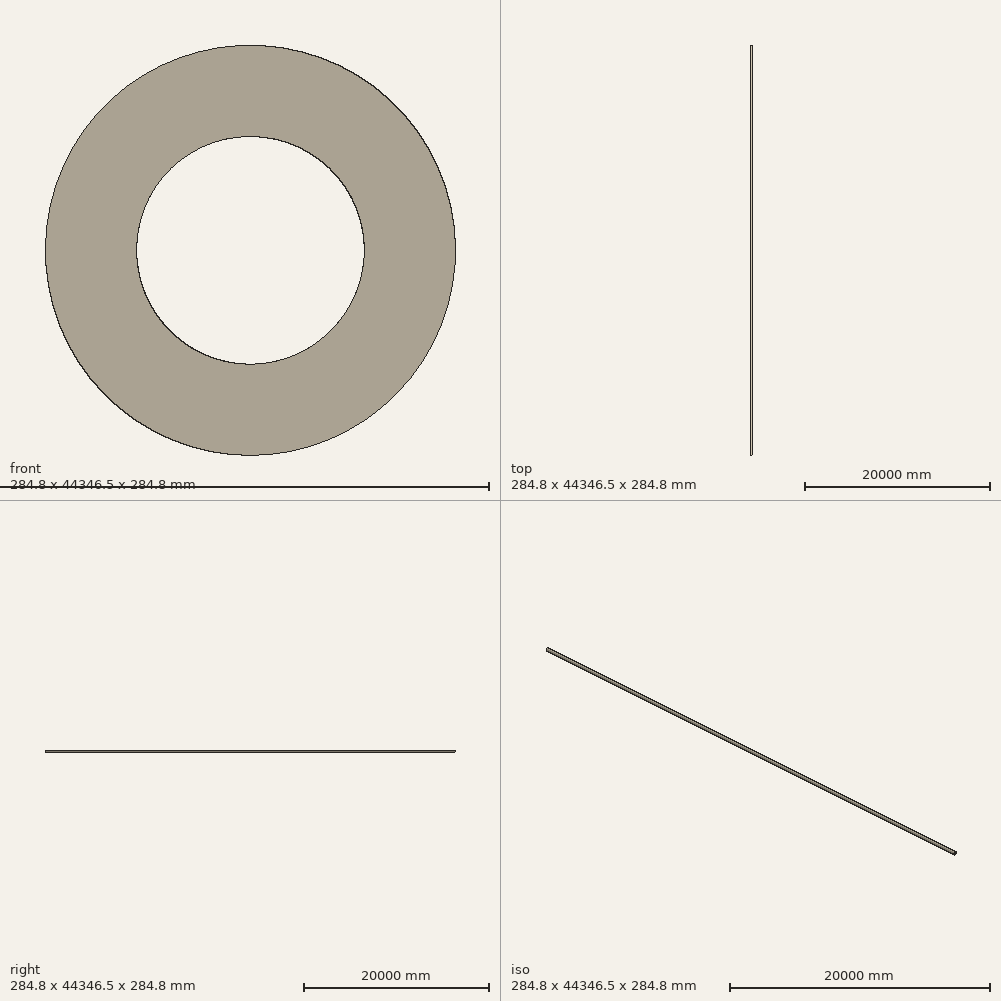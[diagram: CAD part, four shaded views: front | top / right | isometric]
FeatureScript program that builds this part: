
annotation { "Feature Type Name" : "Feature", "Feature Type Description" : "" }
export const myFeature = defineFeature(function(context is Context, id is Id, definition is map)
    precondition{}
    {
        {
            var Q0;
            Q0=qCreatedBy(makeId("Front.planeOp"),FACE);
            var sketch = newSketch(context, id + "F0", { "sketchPlane" : qUnion([Q0])});
            skCircle(sketch, "E0", {"center": v(0, 0) * mm, "radius": 142.38 * mm});
            skSolve(sketch);
        }
        {
            var Q0;
            Q0=makeQuery(id+"F0.imprint","IMPRINT",FACE,{"disambiguationData":[TD([[makeQuery(id+"F0.imprint","IMPRINT",EDGE,{"derivedFrom":sQuery(id+"F0.wireOp",EDGE,"E0")}),1.0]])]});
            extrude(context, id + "F1", {"entities" : qUnion([Q0]), "depth" : 44346.5 * mm, "offsetDistance" : 25.4 * mm});
        }
        {
            var Q0;
            Q0=makeQuery(id+"F1.opExtrude","CAP_FACE",FACE,{"disambiguationData":[OSD([sQuery(id+"F0.wireOp",EDGE,"E0")])],"isStart":true});
            var sketch = newSketch(context, id + "F2", { "sketchPlane" : qUnion([Q0])});
            skCircle(sketch, "E1", {"center": v(0, 0) * mm, "radius": 79.07 * mm});
            skSolve(sketch);
        }
        {
            var Q0;
            Q0=makeQuery(id+"F2.imprint","IMPRINT",FACE,{"disambiguationData":[TD([[makeQuery(id+"F2.imprint","IMPRINT",EDGE,{"derivedFrom":sQuery(id+"F2.wireOp",EDGE,"E1")}),1.0]])]});
            var Q1;
            Q1=sQuery(id+"F2.wireOp",EDGE,"E1");
            extrude(context, id + "F3", {"entities" : qUnion([Q0]), "operationType" : NewBodyOperationType.REMOVE, "surfaceEntities" : qUnion([Q1]), "endBound" : BoundingType.THROUGH_ALL, "oppositeDirection" : true, "depth" : 25.4 * mm, "offsetDistance" : 25.4 * mm});
        }
    });
